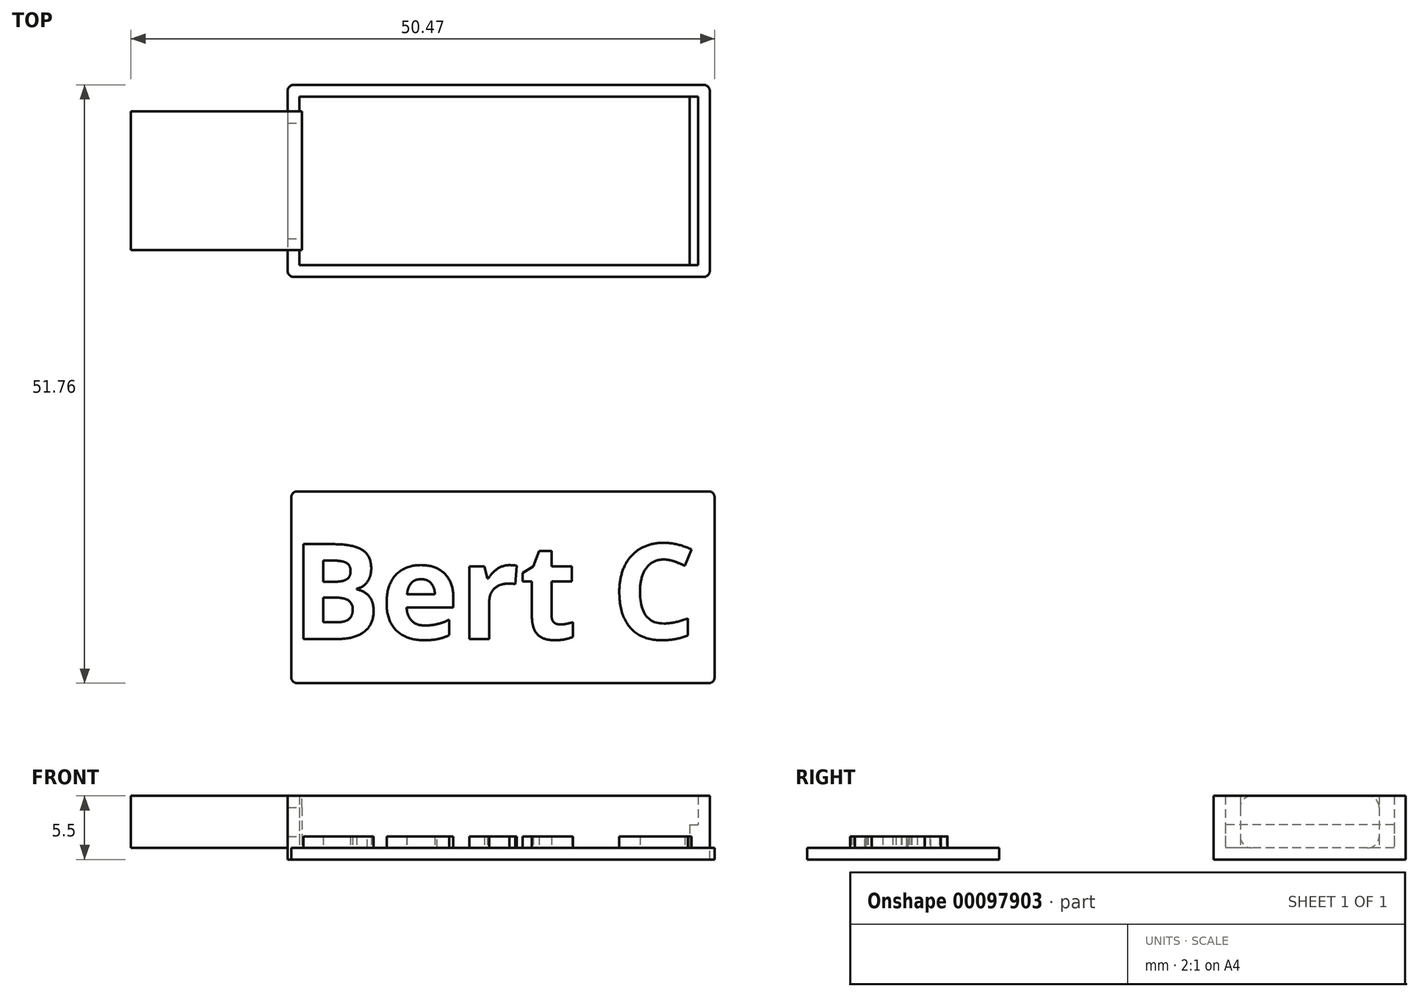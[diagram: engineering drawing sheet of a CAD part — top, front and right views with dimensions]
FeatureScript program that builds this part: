
annotation { "Feature Type Name" : "Feature", "Feature Type Description" : "" }
export const myFeature = defineFeature(function(context is Context, id is Id, definition is map)
    precondition{}
    {
        {
            var Q0;
            Q0=qCreatedBy(makeId("Top.planeOp"),FACE);
            var sketch = newSketch(context, id + "F0", { "sketchPlane" : qUnion([Q0])});
            skLineSegment(sketch, "E0.bottom", {"start": v(-20.83, 2.71) * mm, "end": v(13.17, 2.71) * mm});
            skLineSegment(sketch, "E0.top", {"start": v(-20.83, -11.39) * mm, "end": v(13.17, -11.39) * mm});
            skLineSegment(sketch, "E0.left", {"start": v(-20.83, 2.71) * mm, "end": v(-20.83, -11.39) * mm});
            skLineSegment(sketch, "E0.right", {"start": v(13.17, 2.71) * mm, "end": v(13.17, -11.39) * mm});
            skPoint(sketch, "E1", {"position": v(-20.83, -4.34) * mm});
            skLineSegment(sketch, "E2", {"start": v(-20.83, -4.34) * mm, "end": v(-35.63, -4.34) * mm});
            skLineSegment(sketch, "E3", {"start": v(-35.63, -4.34) * mm, "end": v(-35.63, 1.66) * mm});
            skLineSegment(sketch, "E4", {"start": v(-35.63, 1.66) * mm, "end": v(-20.83, 1.66) * mm});
            skLineSegment(sketch, "E5", {"start": v(-35.63, -4.34) * mm, "end": v(-35.63, -10.34) * mm});
            skLineSegment(sketch, "E6", {"start": v(-35.63, -10.34) * mm, "end": v(-20.83, -10.34) * mm});
            skSolve(sketch);
        }
        {
            var Q0;
            {var subQ0=sQuery(id+"F0.wireOp",EDGE,"E2");Q0=makeQuery(id+"F0.imprint","IMPRINT",FACE,{"disambiguationData":[TD([[makeQuery(id+"F0.imprint","IMPRINT",EDGE,{"derivedFrom":subQ0}),-1.0]])]});}
            var Q1;
            {var subQ0=sQuery(id+"F0.wireOp",EDGE,"E2");Q1=makeQuery(id+"F0.imprint","IMPRINT",FACE,{"disambiguationData":[TD([[makeQuery(id+"F0.imprint","IMPRINT",EDGE,{"derivedFrom":subQ0}),1.0]])]});}
            extrude(context, id + "F1", {"entities" : qUnion([Q0, Q1]), "depth" : 4.5 * mm});
        }
        {
            var Q0;
            Q0=makeQuery(id+"F1.opExtrude","CAP_EDGE",EDGE,{"disambiguationData":[OSD([sQuery(id+"F0.wireOp",EDGE,"E4")])],"isStart":false});
            var Q1;
            Q1=makeQuery(id+"F1.opExtrude","CAP_EDGE",EDGE,{"disambiguationData":[OSD([sQuery(id+"F0.wireOp",EDGE,"E4")])],"isStart":true});
            var Q2;
            Q2=makeQuery(id+"F1.opExtrude","CAP_EDGE",EDGE,{"disambiguationData":[OSD([sQuery(id+"F0.wireOp",EDGE,"E6")])],"isStart":false});
            var Q3;
            Q3=makeQuery(id+"F1.opExtrude","CAP_EDGE",EDGE,{"disambiguationData":[OSD([sQuery(id+"F0.wireOp",EDGE,"E6")])],"isStart":true});
            fillet(context, id + "F2", {"entities" : qUnion([Q0, Q1, Q2, Q3]), "radius" : 1 * mm, "tangentPropagation" : true, "allowEdgeOverflow" : false});
        }
        {
            var Q0;
            {var subQ3=sQuery(id+"F0.wireOp",EDGE,"E0.bottom");Q0=makeQuery(id+"F0.imprint","IMPRINT",FACE,{"disambiguationData":[TD([[makeQuery(id+"F0.imprint","IMPRINT",EDGE,{"derivedFrom":subQ3}),-1.0]])]});}
            var sketch = newSketch(context, id + "F3", { "sketchPlane" : qUnion([Q0])});
            skLineSegment(sketch, "E7.0", {"start": v(-20.83, 2.71) * mm, "end": v(13.17, 2.71) * mm});
            skLineSegment(sketch, "E7.1", {"start": v(-20.83, 2.71) * mm, "end": v(-20.83, -11.39) * mm});
            skLineSegment(sketch, "E7.2", {"start": v(-20.83, -11.39) * mm, "end": v(13.17, -11.39) * mm});
            skLineSegment(sketch, "E7.3", {"start": v(13.17, 2.71) * mm, "end": v(13.17, -11.39) * mm});
            skLineSegment(sketch, "E7.4", {"start": v(-35.63, 1.66) * mm, "end": v(-20.83, 1.66) * mm});
            skLineSegment(sketch, "E7.5", {"start": v(-35.63, -4.34) * mm, "end": v(-35.63, 1.66) * mm});
            skLineSegment(sketch, "E7.6", {"start": v(-35.63, -4.34) * mm, "end": v(-35.63, -10.34) * mm});
            skLineSegment(sketch, "E7.7", {"start": v(-35.63, -10.34) * mm, "end": v(-20.83, -10.34) * mm});
            skLineSegment(sketch, "E8.0", {"start": v(-21.08, 2.96) * mm, "end": v(13.42, 2.96) * mm});
            skLineSegment(sketch, "E8.1", {"start": v(-21.08, 2.96) * mm, "end": v(-21.08, -11.64) * mm});
            skLineSegment(sketch, "E8.2", {"start": v(-21.08, -11.64) * mm, "end": v(13.42, -11.64) * mm});
            skLineSegment(sketch, "E8.3", {"start": v(13.42, 2.96) * mm, "end": v(13.42, -11.64) * mm});
            skLineSegment(sketch, "E9.0", {"start": v(-20.83, -10.89) * mm, "end": v(12.67, -10.89) * mm});
            skLineSegment(sketch, "E9.1", {"start": v(12.67, 2.96) * mm, "end": v(12.67, -11.64) * mm});
            skLineSegment(sketch, "E9.2", {"start": v(-20.83, 2.21) * mm, "end": v(12.67, 2.21) * mm});
            skLineSegment(sketch, "E10.0", {"start": v(-22.08, 3.96) * mm, "end": v(14.42, 3.96) * mm});
            skLineSegment(sketch, "E10.1", {"start": v(-22.08, 3.96) * mm, "end": v(-22.08, -12.64) * mm});
            skLineSegment(sketch, "E10.2", {"start": v(-22.08, -12.64) * mm, "end": v(14.42, -12.64) * mm});
            skLineSegment(sketch, "E10.3", {"start": v(14.42, 3.96) * mm, "end": v(14.42, -12.64) * mm});
            skSolve(sketch);
        }
        {
            var Q0;
            {var subQ3=sQuery(id+"F0.wireOp",EDGE,"E0.bottom");Q0=makeQuery(id+"F0.imprint","IMPRINT",FACE,{"disambiguationData":[TD([[makeQuery(id+"F0.imprint","IMPRINT",EDGE,{"derivedFrom":subQ3}),-1.0]])]});}
            var sketch = newSketch(context, id + "F4", { "sketchPlane" : qUnion([Q0])});
            skLineSegment(sketch, "E11.0", {"start": v(-22.08, 3.96) * mm, "end": v(14.42, 3.96) * mm});
            skLineSegment(sketch, "E11.1", {"start": v(-22.08, 3.96) * mm, "end": v(-22.08, -12.64) * mm});
            skLineSegment(sketch, "E11.2", {"start": v(-22.08, -12.64) * mm, "end": v(14.42, -12.64) * mm});
            skLineSegment(sketch, "E11.3", {"start": v(14.42, 3.96) * mm, "end": v(14.42, -12.64) * mm});
            skSolve(sketch);
        }
        {
            var Q0;
            Q0 = qSketchRegion(id + "F4", true);
            extrude(context, id + "F5", {"entities" : qUnion([Q0]), "oppositeDirection" : true, "depth" : 1 * mm});
        }
        {
            var Q0;
            {var subQ11=sQuery(id+"F3.wireOp",EDGE,"E8.0");Q0=makeQuery(id+"F3.imprint","IMPRINT",FACE,{"disambiguationData":[TD([[makeQuery(id+"F3.imprint","IMPRINT",EDGE,{"derivedFrom":subQ11}),1.0]])]});}
            extrude(context, id + "F6", {"entities" : qUnion([Q0]), "operationType" : NewBodyOperationType.ADD, "depth" : 4.5 * mm});
        }
        {
            var Q0;
            {var subQ4=sQuery(id+"F3.wireOp",EDGE,"E7.3");Q0=makeQuery(id+"F3.imprint","IMPRINT",FACE,{"disambiguationData":[TD([[makeQuery(id+"F3.imprint","IMPRINT",EDGE,{"derivedFrom":subQ4}),-1.0]])]});}
            var Q1;
            {var subQ0=sQuery(id+"F3.wireOp",EDGE,"E7.3");Q1=makeQuery(id+"F3.imprint","IMPRINT",FACE,{"disambiguationData":[TD([[makeQuery(id+"F3.imprint","IMPRINT",EDGE,{"derivedFrom":subQ0}),1.0]])]});}
            extrude(context, id + "F7", {"entities" : qUnion([Q0, Q1]), "operationType" : NewBodyOperationType.ADD, "depth" : 2 * mm});
        }
        {
            var Q0;
            Q0=makeQuery(id+"F6.boolean.opBoolean","MERGE",EDGE,{"derivedFrom":[makeQuery(id+"F5.opExtrude","SWEPT_EDGE",EDGE,{"disambiguationData":[OSD([sQuery(id+"F4.wireOp",EDGE,"E11.1"),sQuery(id+"F4.wireOp",EDGE,"E11.2")])]}),makeQuery(id+"F6.opExtrude","SWEPT_EDGE",EDGE,{"disambiguationData":[OSD([sQuery(id+"F3.wireOp",EDGE,"E10.1"),sQuery(id+"F3.wireOp",EDGE,"E10.2")])]})]});
            var Q1;
            Q1=makeQuery(id+"F6.boolean.opBoolean","MERGE",EDGE,{"derivedFrom":[makeQuery(id+"F5.opExtrude","SWEPT_EDGE",EDGE,{"disambiguationData":[OSD([sQuery(id+"F4.wireOp",EDGE,"E11.0"),sQuery(id+"F4.wireOp",EDGE,"E11.1")])]}),makeQuery(id+"F6.opExtrude","SWEPT_EDGE",EDGE,{"disambiguationData":[OSD([sQuery(id+"F3.wireOp",EDGE,"E10.0"),sQuery(id+"F3.wireOp",EDGE,"E10.1")])]})]});
            var Q2;
            Q2=makeQuery(id+"F6.boolean.opBoolean","MERGE",EDGE,{"derivedFrom":[makeQuery(id+"F5.opExtrude","SWEPT_EDGE",EDGE,{"disambiguationData":[OSD([sQuery(id+"F4.wireOp",EDGE,"E11.0"),sQuery(id+"F4.wireOp",EDGE,"E11.3")])]}),makeQuery(id+"F6.opExtrude","SWEPT_EDGE",EDGE,{"disambiguationData":[OSD([sQuery(id+"F3.wireOp",EDGE,"E10.0"),sQuery(id+"F3.wireOp",EDGE,"E10.3")])]})]});
            var Q3;
            Q3=makeQuery(id+"F6.boolean.opBoolean","MERGE",EDGE,{"derivedFrom":[makeQuery(id+"F5.opExtrude","SWEPT_EDGE",EDGE,{"disambiguationData":[OSD([sQuery(id+"F4.wireOp",EDGE,"E11.2"),sQuery(id+"F4.wireOp",EDGE,"E11.3")])]}),makeQuery(id+"F6.opExtrude","SWEPT_EDGE",EDGE,{"disambiguationData":[OSD([sQuery(id+"F3.wireOp",EDGE,"E10.2"),sQuery(id+"F3.wireOp",EDGE,"E10.3")])]})]});
            fillet(context, id + "F8", {"entities" : qUnion([Q0, Q1, Q2, Q3]), "radius" : .5 * mm, "tangentPropagation" : true, "allowEdgeOverflow" : false});
        }
        {
            var Q0;
            {var subQ4=sQuery(id+"F3.wireOp",EDGE,"E9.0");Q0=makeQuery(id+"F3.imprint","IMPRINT",FACE,{"disambiguationData":[TD([[makeQuery(id+"F3.imprint","IMPRINT",EDGE,{"derivedFrom":subQ4}),1.0]])]});}
            var sketch = newSketch(context, id + "F9", { "sketchPlane" : qUnion([Q0])});
            skLineSegment(sketch, "E12.bottom", {"start": v(-21.76, -31.2) * mm, "end": v(14.84, -31.2) * mm});
            skLineSegment(sketch, "E12.top", {"start": v(-21.76, -47.8) * mm, "end": v(14.84, -47.8) * mm});
            skLineSegment(sketch, "E12.left", {"start": v(-21.76, -31.2) * mm, "end": v(-21.76, -47.8) * mm});
            skLineSegment(sketch, "E12.right", {"start": v(14.84, -31.2) * mm, "end": v(14.84, -47.8) * mm});
            skText(sketch, "E13", { "text": "Bert C\n", "fontName": "OpenSans-Bold.ttf"});
            const initialGuessF9  = {"E13": [-0.02176, -0.04397, 1, 0, 0.00827]};
            skSetInitialGuess(sketch, initialGuessF9);
            skSolve(sketch);
        }
        {
            var Q0;
            Q0=makeQuery(id+"F9.imprint","IMPRINT",FACE,{"disambiguationData":[TD([[makeQuery(id+"F9.imprint","IMPRINT",EDGE,{"derivedFrom":sQuery(id+"F9.wireOp",EDGE,"E13.sketch_text.stroke-0")}),-1.0]])]});
            var Q1;
            Q1=makeQuery(id+"F9.imprint","IMPRINT",FACE,{"disambiguationData":[TD([[makeQuery(id+"F9.imprint","IMPRINT",EDGE,{"derivedFrom":sQuery(id+"F9.wireOp",EDGE,"E12.bottom")}),-1.0]])]});
            var Q2;
            Q2=makeQuery(id+"F9.imprint","IMPRINT",FACE,{"disambiguationData":[TD([[makeQuery(id+"F9.imprint","IMPRINT",EDGE,{"derivedFrom":sQuery(id+"F9.wireOp",EDGE,"E13.sketch_text.stroke-19")}),1.0]])]});
            var Q3;
            Q3=makeQuery(id+"F9.imprint","IMPRINT",FACE,{"disambiguationData":[TD([[makeQuery(id+"F9.imprint","IMPRINT",EDGE,{"derivedFrom":sQuery(id+"F9.wireOp",EDGE,"E13.sketch_text.stroke-12")}),1.0]])]});
            var Q4;
            Q4=makeQuery(id+"F9.imprint","IMPRINT",FACE,{"disambiguationData":[TD([[makeQuery(id+"F9.imprint","IMPRINT",EDGE,{"derivedFrom":sQuery(id+"F9.wireOp",EDGE,"E13.sketch_text.stroke-25")}),-1.0]])]});
            var Q5;
            Q5=makeQuery(id+"F9.imprint","IMPRINT",FACE,{"disambiguationData":[TD([[makeQuery(id+"F9.imprint","IMPRINT",EDGE,{"derivedFrom":sQuery(id+"F9.wireOp",EDGE,"E13.sketch_text.stroke-25")}),1.0]])]});
            var Q6;
            Q6=makeQuery(id+"F9.imprint","IMPRINT",FACE,{"disambiguationData":[TD([[makeQuery(id+"F9.imprint","IMPRINT",EDGE,{"derivedFrom":sQuery(id+"F9.wireOp",EDGE,"E13.sketch_text.stroke-45")}),-1.0]])]});
            var Q7;
            Q7=makeQuery(id+"F9.imprint","IMPRINT",FACE,{"disambiguationData":[TD([[makeQuery(id+"F9.imprint","IMPRINT",EDGE,{"derivedFrom":sQuery(id+"F9.wireOp",EDGE,"E13.sketch_text.stroke-58")}),-1.0]])]});
            var Q8;
            Q8=makeQuery(id+"F9.imprint","IMPRINT",FACE,{"disambiguationData":[TD([[makeQuery(id+"F9.imprint","IMPRINT",EDGE,{"derivedFrom":sQuery(id+"F9.wireOp",EDGE,"E13.sketch_text.stroke-76")}),-1.0]])]});
            extrude(context, id + "F10", {"entities" : qUnion([Q0, Q1, Q2, Q3, Q4, Q5, Q6, Q7, Q8]), "oppositeDirection" : true, "depth" : 1 * mm});
        }
        {
            var Q0;
            Q0=makeQuery(id+"F9.imprint","IMPRINT",FACE,{"disambiguationData":[TD([[makeQuery(id+"F9.imprint","IMPRINT",EDGE,{"derivedFrom":sQuery(id+"F9.wireOp",EDGE,"E13.sketch_text.stroke-0")}),-1.0]])]});
            var Q1;
            Q1=makeQuery(id+"F9.imprint","IMPRINT",FACE,{"disambiguationData":[TD([[makeQuery(id+"F9.imprint","IMPRINT",EDGE,{"derivedFrom":sQuery(id+"F9.wireOp",EDGE,"E13.sketch_text.stroke-25")}),-1.0]])]});
            var Q2;
            Q2=makeQuery(id+"F9.imprint","IMPRINT",FACE,{"disambiguationData":[TD([[makeQuery(id+"F9.imprint","IMPRINT",EDGE,{"derivedFrom":sQuery(id+"F9.wireOp",EDGE,"E13.sketch_text.stroke-45")}),-1.0]])]});
            var Q3;
            Q3=makeQuery(id+"F9.imprint","IMPRINT",FACE,{"disambiguationData":[TD([[makeQuery(id+"F9.imprint","IMPRINT",EDGE,{"derivedFrom":sQuery(id+"F9.wireOp",EDGE,"E13.sketch_text.stroke-58")}),-1.0]])]});
            var Q4;
            Q4=makeQuery(id+"F9.imprint","IMPRINT",FACE,{"disambiguationData":[TD([[makeQuery(id+"F9.imprint","IMPRINT",EDGE,{"derivedFrom":sQuery(id+"F9.wireOp",EDGE,"E13.sketch_text.stroke-76")}),-1.0]])]});
            extrude(context, id + "F11", {"entities" : qUnion([Q0, Q1, Q2, Q3, Q4]), "operationType" : NewBodyOperationType.ADD, "depth" : 1 * mm});
        }
        {
            var Q0;
            Q0=makeQuery(id+"F10.opExtrude","SWEPT_EDGE",EDGE,{"disambiguationData":[OSD([sQuery(id+"F9.wireOp",EDGE,"E12.top"),sQuery(id+"F9.wireOp",EDGE,"E12.left")])]});
            var Q1;
            Q1=makeQuery(id+"F10.opExtrude","SWEPT_EDGE",EDGE,{"disambiguationData":[OSD([sQuery(id+"F9.wireOp",EDGE,"E12.top"),sQuery(id+"F9.wireOp",EDGE,"E12.right")])]});
            var Q2;
            Q2=makeQuery(id+"F10.opExtrude","SWEPT_EDGE",EDGE,{"disambiguationData":[OSD([sQuery(id+"F9.wireOp",EDGE,"E12.bottom"),sQuery(id+"F9.wireOp",EDGE,"E12.right")])]});
            var Q3;
            Q3=makeQuery(id+"F10.opExtrude","SWEPT_EDGE",EDGE,{"disambiguationData":[OSD([sQuery(id+"F9.wireOp",EDGE,"E12.bottom"),sQuery(id+"F9.wireOp",EDGE,"E12.left")])]});
            fillet(context, id + "F12", {"entities" : qUnion([Q0, Q1, Q2, Q3]), "radius" : .5 * mm, "tangentPropagation" : true, "allowEdgeOverflow" : false});
        }
    });
